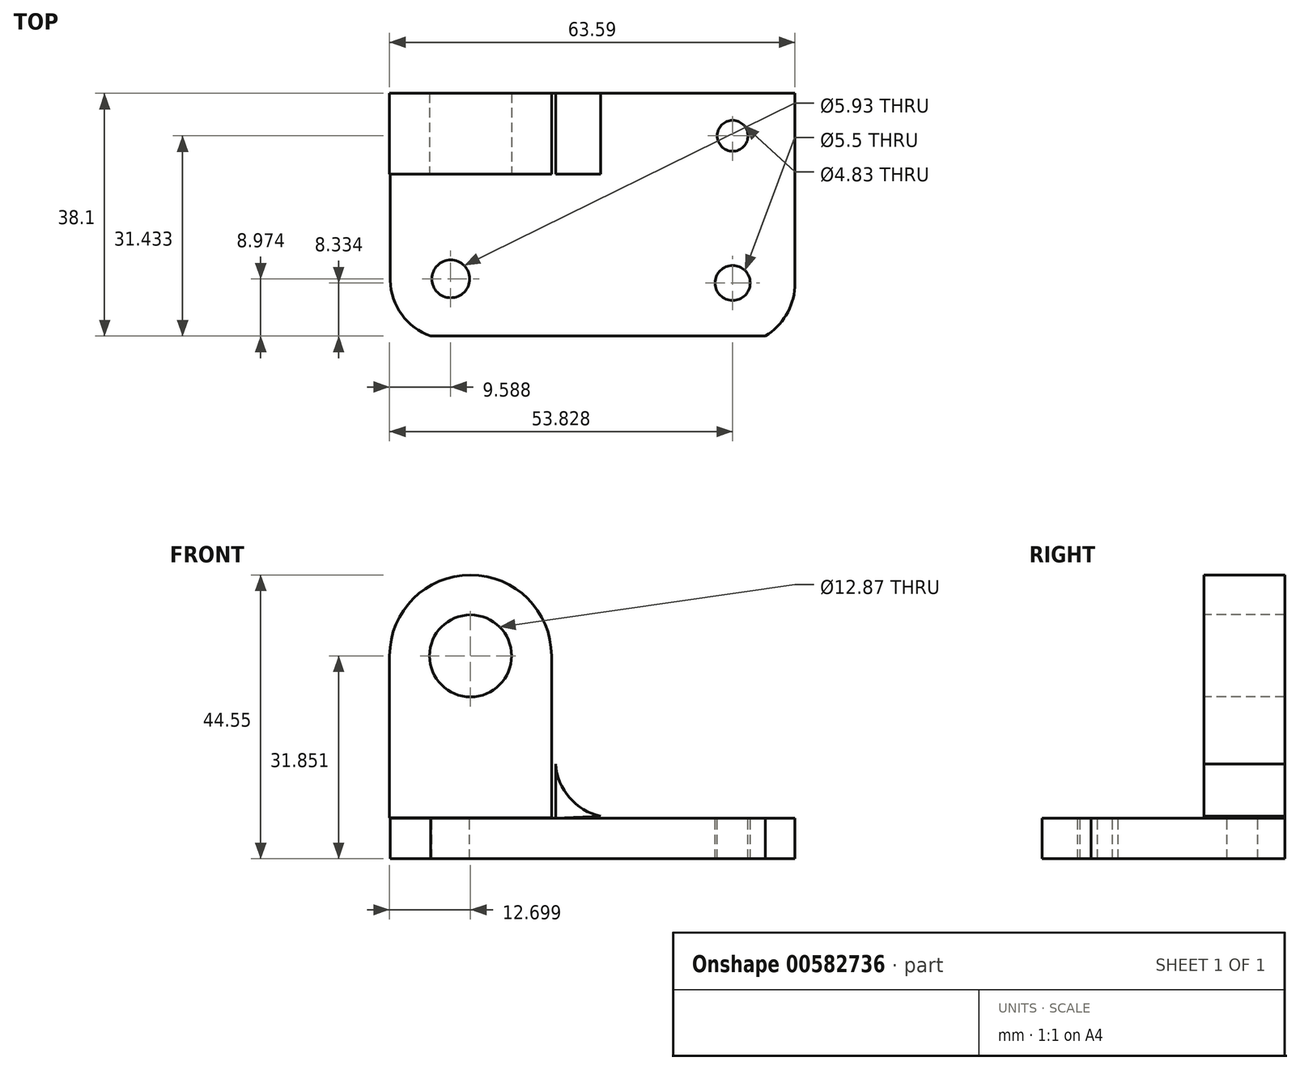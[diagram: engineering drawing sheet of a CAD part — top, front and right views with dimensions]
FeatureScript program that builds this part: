
annotation { "Feature Type Name" : "Feature", "Feature Type Description" : "" }
export const myFeature = defineFeature(function(context is Context, id is Id, definition is map)
    precondition{}
    {
        {
            var Q0;
            Q0=qCreatedBy(makeId("Front.planeOp"),FACE);
            var sketch = newSketch(context, id + "F0", { "sketchPlane" : qUnion([Q0])});
            skLineSegment(sketch, "E0", {"start": v(-70.63, 0) * mm, "end": v(-7.13, 0) * mm});
            skLineSegment(sketch, "E1", {"start": v(-7.13, 0) * mm, "end": v(-7.13, 6.35) * mm});
            skLineSegment(sketch, "E2", {"start": v(-7.13, 6.35) * mm, "end": v(-70.63, 6.35) * mm});
            skLineSegment(sketch, "E3", {"start": v(-70.63, 6.35) * mm, "end": v(-70.63, 0) * mm});
            skSolve(sketch);
        }
        {
            var Q0;
            Q0=makeQuery(id+"F0.imprint","IMPRINT",FACE,{"disambiguationData":[TD([[makeQuery(id+"F0.imprint","IMPRINT",EDGE,{"derivedFrom":sQuery(id+"F0.wireOp",EDGE,"E0")}),1.0]])]});
            extrude(context, id + "F1", {"entities" : qUnion([Q0]), "depth" : 38.1 * mm, "offsetDistance" : 25.4 * mm});
        }
        {
            var Q0;
            Q0=qCreatedBy(makeId("Front.planeOp"),FACE);
            var sketch = newSketch(context, id + "F2", { "sketchPlane" : qUnion([Q0])});
            skLineSegment(sketch, "E4", {"start": v(-70.72, 6.45) * mm, "end": v(-70.72, 31.85) * mm});
            skLineSegment(sketch, "E5", {"start": v(-70.72, 31.85) * mm, "end": v(-45.32, 31.85) * mm});
            skLineSegment(sketch, "E6", {"start": v(-45.32, 31.85) * mm, "end": v(-45.32, 6.45) * mm});
            skLineSegment(sketch, "E7", {"start": v(-70.72, 6.45) * mm, "end": v(-45.32, 6.45) * mm});
            skArc(sketch, "E8", {"start": v(-45.32, 31.85) * mm, "mid": v(-58.02, 44.55) * mm, "end": v(-70.72, 31.85) * mm});
            skSolve(sketch);
        }
        {
            var Q0;
            Q0=makeQuery(id+"F2.imprint","IMPRINT",FACE,{"disambiguationData":[TD([[makeQuery(id+"F2.imprint","IMPRINT",EDGE,{"derivedFrom":sQuery(id+"F2.wireOp",EDGE,"E5")}),1.0]])]});
            var Q1;
            Q1=makeQuery(id+"F2.imprint","IMPRINT",FACE,{"disambiguationData":[TD([[makeQuery(id+"F2.imprint","IMPRINT",EDGE,{"derivedFrom":sQuery(id+"F2.wireOp",EDGE,"E4")}),-1.0]])]});
            extrude(context, id + "F3", {"entities" : qUnion([Q0, Q1]), "depth" : 12.7 * mm, "offsetDistance" : 25.4 * mm});
        }
        {
            var Q0;
            Q0=qCreatedBy(makeId("Front.planeOp"),FACE);
            var sketch = newSketch(context, id + "F4", { "sketchPlane" : qUnion([Q0])});
            skArc(sketch, "E9", {"start": v(-44.69, 14.9) * mm, "mid": v(-42.5, 9.61) * mm, "end": v(-37.6, 6.67) * mm});
            skLineSegment(sketch, "E10", {"start": v(-44.69, 14.9) * mm, "end": v(-44.69, 6.38) * mm});
            skLineSegment(sketch, "E11", {"start": v(-44.69, 6.38) * mm, "end": v(-37.6, 6.67) * mm});
            skSolve(sketch);
        }
        {
            var Q0;
            Q0=makeQuery(id+"F4.imprint","IMPRINT",FACE,{"disambiguationData":[TD([[makeQuery(id+"F4.imprint","IMPRINT",EDGE,{"derivedFrom":sQuery(id+"F4.wireOp",EDGE,"E9")}),-1.0]])]});
            extrude(context, id + "F5", {"entities" : qUnion([Q0]), "depth" : 12.7 * mm, "offsetDistance" : 25.4 * mm});
        }
        {
            var Q0;
            Q0=makeQuery(id+"F1.opExtrude","SWEPT_FACE",FACE,{"disambiguationData":[OSD([sQuery(id+"F0.wireOp",EDGE,"E2")])]});
            var sketch = newSketch(context, id + "F6", { "sketchPlane" : qUnion([Q0])});
            skArc(sketch, "E12", {"start": v(-70.63, -29.37) * mm, "mid": v(-68.81, -34.73) * mm, "end": v(-64.26, -38.1) * mm});
            skArc(sketch, "E13", {"start": v(-11.77, -38.1) * mm, "mid": v(-8.2, -34.26) * mm, "end": v(-7.13, -29.13) * mm});
            skSolve(sketch);
        }
        {
            var Q0;
            {var subQ0=sQuery(id+"F6.wireOp",EDGE,"E12");Q0=makeQuery(id+"F6.imprint","IMPRINT",FACE,{"disambiguationData":[TD([[makeQuery(id+"F6.imprint","IMPRINT",EDGE,{"derivedFrom":subQ0}),-1.0]])]});}
            var Q1;
            {var subQ0=sQuery(id+"F6.wireOp",EDGE,"E13");var subQ1=sQuery(id+"F0.wireOp",EDGE,"E2");var subQ2=makeQuery(id+"F1.opExtrude","CAP_EDGE",EDGE,{"disambiguationData":[OSD([subQ1])],"isStart":false});var subQ3=makeQuery(id+"F6.imprint","INTERSECT",VERTEX,{"derivedFrom":[subQ2,subQ0]});Q1=makeQuery(id+"F6.imprint","IMPRINT",FACE,{"disambiguationData":[TD([[makeQuery(id+"F6.imprint","IMPRINT",EDGE,{"disambiguationData":[TD([[subQ3,-1.0]])],"derivedFrom":subQ0}),-1.0]])]});}
            extrude(context, id + "F7", {"entities" : qUnion([Q0, Q1]), "operationType" : NewBodyOperationType.REMOVE, "oppositeDirection" : true, "depth" : 6.35 * mm, "offsetDistance" : 25.4 * mm});
        }
        {
            var Q0;
            Q0=makeQuery(id+"F3.opExtrude","CAP_FACE",FACE,{"disambiguationData":[OSD([sQuery(id+"F2.wireOp",EDGE,"E4"),sQuery(id+"F2.wireOp",EDGE,"E6"),sQuery(id+"F2.wireOp",EDGE,"E7"),sQuery(id+"F2.wireOp",EDGE,"E8")])],"isStart":false});
            var sketch = newSketch(context, id + "F8", { "sketchPlane" : qUnion([Q0])});
            skCircle(sketch, "E14", {"center": v(-58.02, 31.85) * mm, "radius": 6.43 * mm});
            skSolve(sketch);
        }
        {
            var Q0;
            Q0=makeQuery(id+"F8.imprint","IMPRINT",FACE,{"disambiguationData":[TD([[makeQuery(id+"F8.imprint","IMPRINT",EDGE,{"derivedFrom":sQuery(id+"F8.wireOp",EDGE,"E14")}),1.0]])]});
            extrude(context, id + "F9", {"entities" : qUnion([Q0]), "operationType" : NewBodyOperationType.REMOVE, "oppositeDirection" : true, "depth" : 12.7 * mm, "offsetDistance" : 25.4 * mm});
        }
        {
            var Q0;
            Q0=makeQuery(id+"F1.opExtrude","SWEPT_FACE",FACE,{"disambiguationData":[OSD([sQuery(id+"F0.wireOp",EDGE,"E2")])]});
            var sketch = newSketch(context, id + "F10", { "sketchPlane" : qUnion([Q0])});
            skCircle(sketch, "E15", {"center": v(-61.13, -29.13) * mm, "radius": 2.96 * mm});
            skCircle(sketch, "E16", {"center": v(-16.9, -29.77) * mm, "radius": 2.75 * mm});
            skCircle(sketch, "E17", {"center": v(-16.9, -6.67) * mm, "radius": 2.41 * mm});
            skSolve(sketch);
        }
        {
            var Q0;
            Q0=makeQuery(id+"F10.imprint","IMPRINT",FACE,{"disambiguationData":[TD([[makeQuery(id+"F10.imprint","IMPRINT",EDGE,{"derivedFrom":sQuery(id+"F10.wireOp",EDGE,"E17")}),1.0]])]});
            var Q1;
            Q1=makeQuery(id+"F10.imprint","IMPRINT",FACE,{"disambiguationData":[TD([[makeQuery(id+"F10.imprint","IMPRINT",EDGE,{"derivedFrom":sQuery(id+"F10.wireOp",EDGE,"E16")}),1.0]])]});
            var Q2;
            Q2=makeQuery(id+"F10.imprint","IMPRINT",FACE,{"disambiguationData":[TD([[makeQuery(id+"F10.imprint","IMPRINT",EDGE,{"derivedFrom":sQuery(id+"F10.wireOp",EDGE,"E15")}),1.0]])]});
            extrude(context, id + "F11", {"entities" : qUnion([Q0, Q1, Q2]), "operationType" : NewBodyOperationType.REMOVE, "oppositeDirection" : true, "depth" : 6.35 * mm, "offsetDistance" : 25.4 * mm});
        }
    });
